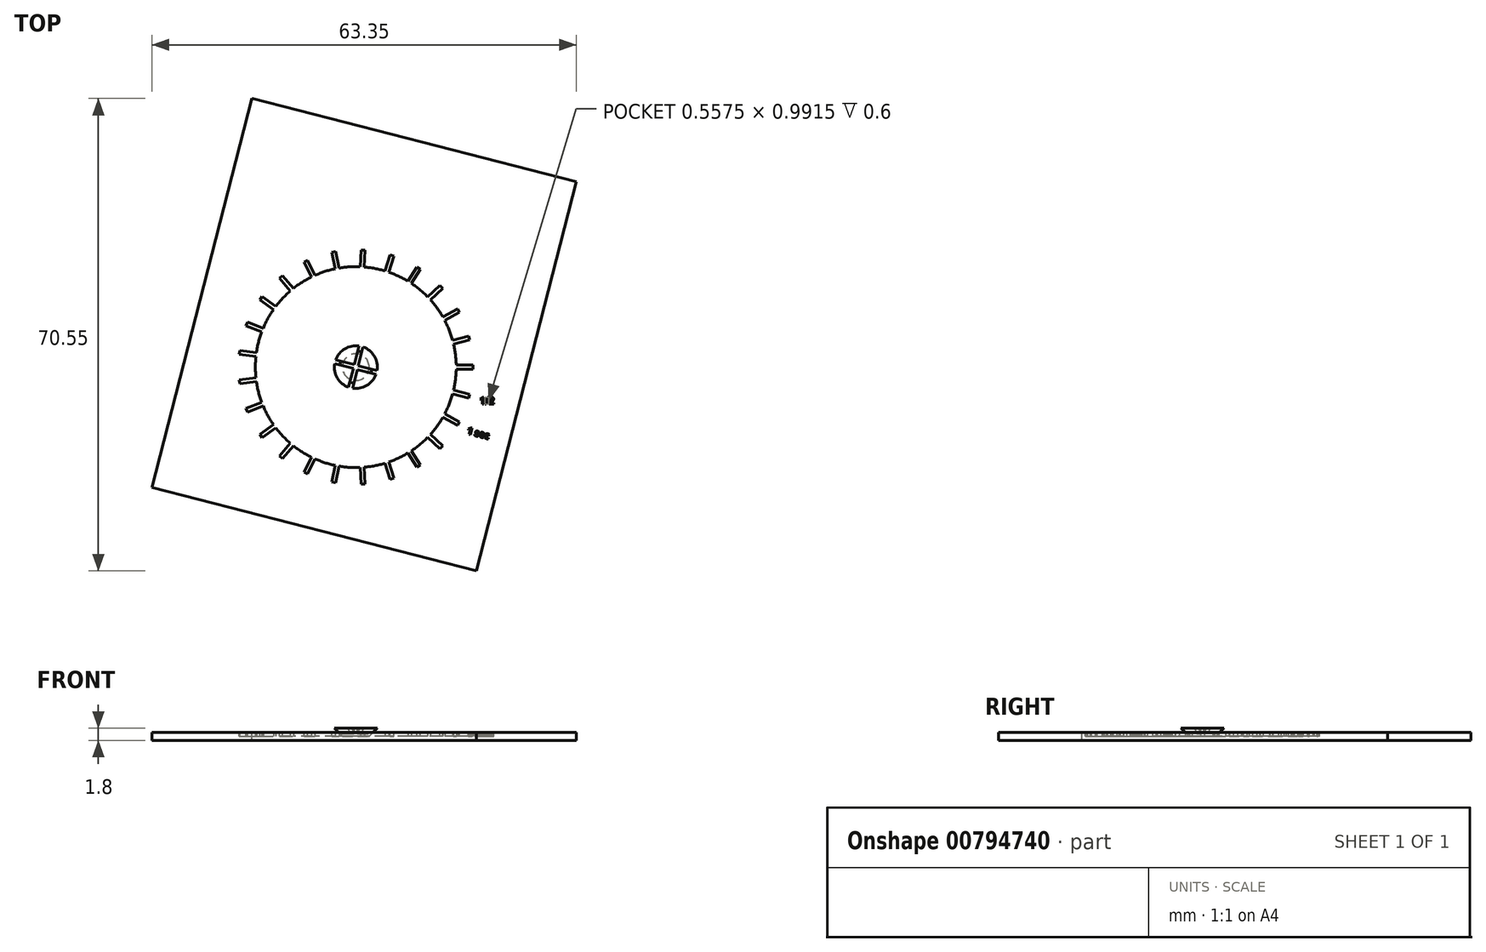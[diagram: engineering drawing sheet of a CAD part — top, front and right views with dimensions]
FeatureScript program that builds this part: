
annotation { "Feature Type Name" : "Feature", "Feature Type Description" : "" }
export const myFeature = defineFeature(function(context is Context, id is Id, definition is map)
    precondition{}
    {
        {
            var Q0;
            Q0=qCreatedBy(makeId("Top.planeOp"),FACE);
            var sketch = newSketch(context, id + "F0", { "sketchPlane" : qUnion([Q0])});
            skLineSegment(sketch, "E0.bottom", {"start": v(25, -30) * mm, "end": v(-25, -30) * mm});
            skLineSegment(sketch, "E0.top", {"start": v(25, 30) * mm, "end": v(-25, 30) * mm});
            skLineSegment(sketch, "E0.left", {"start": v(25, -30) * mm, "end": v(25, 30) * mm});
            skLineSegment(sketch, "E0.right", {"start": v(-25, -30) * mm, "end": v(-25, 30) * mm});
            skPoint(sketch, "E0.middle", {"position": v(0, 0) * mm});
            skCircle(sketch, "E1", {"center": v(0, -5) * mm, "radius": 15 * mm});
            skLineSegment(sketch, "E2", {"start": v(70, 36.13) * mm, "end": v(70, -44.16) * mm, "construction": true});
            skCircle(sketch, "E3", {"center": v(70, -12.38) * mm, "radius": 14.5 * mm});
            skLineSegment(sketch, "E4", {"start": v(70, -12.38) * mm, "end": v(87.5, -12.38) * mm, "construction": true});
            skLineSegment(sketch, "E5.bottom", {"start": v(82, -12.08) * mm, "end": v(87, -12.08) * mm});
            skLineSegment(sketch, "E5.top", {"start": v(82, -12.68) * mm, "end": v(87, -12.68) * mm});
            skLineSegment(sketch, "E5.left", {"start": v(82, -12.08) * mm, "end": v(82, -12.68) * mm});
            skLineSegment(sketch, "E5.right", {"start": v(87, -12.08) * mm, "end": v(87, -12.68) * mm});
            skSolve(sketch);
        }
        {
            var Q0;
            Q0=qCreatedBy(makeId("Right.planeOp"),FACE);
            var sketch = newSketch(context, id + "F1", { "sketchPlane" : qUnion([Q0])});
            skLineSegment(sketch, "E6", {"start": v(-5, 57.83) * mm, "end": v(-5, -48.42) * mm, "construction": true});
            skSolve(sketch);
        }
        {
            var Q0;
            Q0=makeQuery(id+"F0.imprint","IMPRINT",FACE,{"disambiguationData":[TD([[makeQuery(id+"F0.imprint","IMPRINT",EDGE,{"derivedFrom":sQuery(id+"F0.wireOp",EDGE,"E0.bottom")}),-1.0]])]});
            var Q1;
            Q1=makeQuery(id+"F0.imprint","IMPRINT",FACE,{"disambiguationData":[TD([[makeQuery(id+"F0.imprint","IMPRINT",EDGE,{"derivedFrom":sQuery(id+"F0.wireOp",EDGE,"E1")}),1.0]])]});
            extrude(context, id + "F2", {"entities" : qUnion([Q0, Q1]), "oppositeDirection" : true, "depth" : 0.6 * mm, "offsetDistance" : 25 * mm});
        }
        {
            var Q0;
            Q0=makeQuery(id+"F0.imprint","IMPRINT",FACE,{"disambiguationData":[TD([[makeQuery(id+"F0.imprint","IMPRINT",EDGE,{"derivedFrom":sQuery(id+"F0.wireOp",EDGE,"E0.bottom")}),-1.0]])]});
            extrude(context, id + "F3", {"entities" : qUnion([Q0]), "operationType" : NewBodyOperationType.ADD, "depth" : 0.6 * mm, "offsetDistance" : 25 * mm});
        }
        {
            var Q0;
            Q0=makeQuery(id+"F0.imprint","IMPRINT",FACE,{"disambiguationData":[TD([[makeQuery(id+"F0.imprint","IMPRINT",EDGE,{"derivedFrom":sQuery(id+"F0.wireOp",EDGE,"E1")}),1.0]])]});
            var sketch = newSketch(context, id + "F4", { "sketchPlane" : qUnion([Q0])});
            skCircle(sketch, "E7", {"center": v(0, -5) * mm, "radius": 2 * mm});
            skSolve(sketch);
        }
        {
            var Q0;
            Q0=makeQuery(id+"F4.imprint","IMPRINT",FACE,{"disambiguationData":[TD([[makeQuery(id+"F4.imprint","IMPRINT",EDGE,{"derivedFrom":sQuery(id+"F4.wireOp",EDGE,"E7")}),1.0]])]});
            extrude(context, id + "F5", {"entities" : qUnion([Q0]), "operationType" : NewBodyOperationType.ADD, "depth" : 1.2 * mm, "offsetDistance" : 25 * mm, "hasDraft" : true, "draftAngle" : 45 * degree});
        }
        {
            var Q0;
            Q0=makeQuery(id+"F5.opExtrude","CAP_FACE",FACE,{"disambiguationData":[OSD([sQuery(id+"F4.wireOp",EDGE,"E7")])],"isStart":false});
            var sketch = newSketch(context, id + "F6", { "sketchPlane" : qUnion([Q0])});
            skLineSegment(sketch, "E8.bottom", {"start": v(-0.3, 0) * mm, "end": v(0.3, 0) * mm});
            skLineSegment(sketch, "E8.top", {"start": v(-0.3, -10) * mm, "end": v(0.3, -10) * mm});
            skLineSegment(sketch, "E8.left", {"start": v(-0.3, 0) * mm, "end": v(-0.3, -10) * mm});
            skLineSegment(sketch, "E8.right", {"start": v(0.3, 0) * mm, "end": v(0.3, -10) * mm});
            skPoint(sketch, "E8.middle", {"position": v(0, -5) * mm});
            skLineSegment(sketch, "E9.bottom", {"start": v(-5, -4.7) * mm, "end": v(5, -4.7) * mm});
            skLineSegment(sketch, "E9.top", {"start": v(-5, -5.3) * mm, "end": v(5, -5.3) * mm});
            skLineSegment(sketch, "E9.left", {"start": v(-5, -4.7) * mm, "end": v(-5, -5.3) * mm});
            skLineSegment(sketch, "E9.right", {"start": v(5, -4.7) * mm, "end": v(5, -5.3) * mm});
            skSolve(sketch);
        }
        {
            var Q0;
            Q0 = qSketchRegion(id + "F6", true);
            extrude(context, id + "F7", {"entities" : qUnion([Q0]), "operationType" : NewBodyOperationType.REMOVE, "oppositeDirection" : true, "depth" : 0.8 * mm, "offsetDistance" : 25 * mm});
        }
        {
            var Q0;
            Q0=makeQuery(id+"F3.opExtrude","CAP_FACE",FACE,{"disambiguationData":[OSD([sQuery(id+"F0.wireOp",EDGE,"E0.bottom"),sQuery(id+"F0.wireOp",EDGE,"E0.top"),sQuery(id+"F0.wireOp",EDGE,"E0.left"),sQuery(id+"F0.wireOp",EDGE,"E0.right"),sQuery(id+"F0.wireOp",EDGE,"E1")])],"isStart":false});
            var sketch = newSketch(context, id + "F8", { "sketchPlane" : qUnion([Q0])});
            skLineSegment(sketch, "E10", {"start": v(0, 17.05) * mm, "end": v(0, -50.38) * mm, "construction": true});
            skLineSegment(sketch, "E11", {"start": v(-21.67, -5) * mm, "end": v(32.65, -5) * mm, "construction": true});
            skLineSegment(sketch, "E12.bottom", {"start": v(17.5, -4.7) * mm, "end": v(12.5, -4.7) * mm});
            skLineSegment(sketch, "E12.top", {"start": v(17.5, -5.3) * mm, "end": v(12.5, -5.3) * mm});
            skLineSegment(sketch, "E12.left", {"start": v(17.5, -4.7) * mm, "end": v(17.5, -5.3) * mm});
            skLineSegment(sketch, "E12.right", {"start": v(12.5, -4.7) * mm, "end": v(12.5, -5.3) * mm});
            skPoint(sketch, "E12.middle", {"position": v(15, -5) * mm});
            skLineSegment(sketch, "E13.1.0", {"start": v(16.88, -0.36) * mm, "end": v(12.03, -1.6) * mm});
            skLineSegment(sketch, "E13.1.1", {"start": v(17.02, -0.94) * mm, "end": v(12.18, -2.18) * mm});
            skLineSegment(sketch, "E13.1.2", {"start": v(16.88, -0.36) * mm, "end": v(17.02, -0.94) * mm});
            skLineSegment(sketch, "E13.1.3", {"start": v(12.03, -1.6) * mm, "end": v(12.18, -2.18) * mm});
            skLineSegment(sketch, "E13.2.0", {"start": v(15.2, 3.7) * mm, "end": v(10.8, 1.28) * mm});
            skLineSegment(sketch, "E13.2.1", {"start": v(15.48, 3.17) * mm, "end": v(11.1, 0.76) * mm});
            skLineSegment(sketch, "E13.2.2", {"start": v(15.2, 3.7) * mm, "end": v(15.48, 3.17) * mm});
            skLineSegment(sketch, "E13.2.3", {"start": v(10.8, 1.28) * mm, "end": v(11.1, 0.76) * mm});
            skLineSegment(sketch, "E13.3.0", {"start": v(12.55, 7.2) * mm, "end": v(8.9, 3.78) * mm});
            skLineSegment(sketch, "E13.3.1", {"start": v(12.96, 6.76) * mm, "end": v(9.32, 3.34) * mm});
            skLineSegment(sketch, "E13.3.2", {"start": v(12.55, 7.2) * mm, "end": v(12.96, 6.76) * mm});
            skLineSegment(sketch, "E13.3.3", {"start": v(8.9, 3.78) * mm, "end": v(9.32, 3.34) * mm});
            skLineSegment(sketch, "E13.4.0", {"start": v(9.12, 9.94) * mm, "end": v(6.44, 5.71) * mm});
            skLineSegment(sketch, "E13.4.1", {"start": v(9.63, 9.61) * mm, "end": v(6.95, 5.4) * mm});
            skLineSegment(sketch, "E13.4.2", {"start": v(9.12, 9.94) * mm, "end": v(9.63, 9.61) * mm});
            skLineSegment(sketch, "E13.4.3", {"start": v(6.44, 5.71) * mm, "end": v(6.95, 5.4) * mm});
            skLineSegment(sketch, "E13.5.0", {"start": v(5.12, 11.74) * mm, "end": v(3.58, 6.98) * mm});
            skLineSegment(sketch, "E13.5.1", {"start": v(5.7, 11.55) * mm, "end": v(4.15, 6.8) * mm});
            skLineSegment(sketch, "E13.5.2", {"start": v(5.12, 11.74) * mm, "end": v(5.7, 11.55) * mm});
            skLineSegment(sketch, "E13.5.3", {"start": v(3.58, 6.98) * mm, "end": v(4.15, 6.8) * mm});
            skLineSegment(sketch, "E13.6.0", {"start": v(0.8, 12.48) * mm, "end": v(0.49, 7.5) * mm});
            skLineSegment(sketch, "E13.6.1", {"start": v(1.4, 12.45) * mm, "end": v(1.08, 7.46) * mm});
            skLineSegment(sketch, "E13.6.2", {"start": v(0.8, 12.48) * mm, "end": v(1.4, 12.45) * mm});
            skLineSegment(sketch, "E13.6.3", {"start": v(0.49, 7.5) * mm, "end": v(1.08, 7.46) * mm});
            skLineSegment(sketch, "E13.7.0", {"start": v(-3.57, 12.13) * mm, "end": v(-2.64, 7.22) * mm});
            skLineSegment(sketch, "E13.7.1", {"start": v(-2.98, 12.25) * mm, "end": v(-2.05, 7.33) * mm});
            skLineSegment(sketch, "E13.7.2", {"start": v(-3.57, 12.13) * mm, "end": v(-2.98, 12.25) * mm});
            skLineSegment(sketch, "E13.7.3", {"start": v(-2.64, 7.22) * mm, "end": v(-2.05, 7.33) * mm});
            skLineSegment(sketch, "E13.8.0", {"start": v(-7.72, 10.7) * mm, "end": v(-5.6, 6.18) * mm});
            skLineSegment(sketch, "E13.8.1", {"start": v(-7.18, 10.96) * mm, "end": v(-5.05, 6.44) * mm});
            skLineSegment(sketch, "E13.8.2", {"start": v(-7.72, 10.7) * mm, "end": v(-7.18, 10.96) * mm});
            skLineSegment(sketch, "E13.8.3", {"start": v(-5.6, 6.18) * mm, "end": v(-5.05, 6.44) * mm});
            skLineSegment(sketch, "E13.9.0", {"start": v(-11.39, 8.3) * mm, "end": v(-8.2, 4.44) * mm});
            skLineSegment(sketch, "E13.9.1", {"start": v(-10.92, 8.68) * mm, "end": v(-7.74, 4.82) * mm});
            skLineSegment(sketch, "E13.9.2", {"start": v(-11.39, 8.3) * mm, "end": v(-10.92, 8.68) * mm});
            skLineSegment(sketch, "E13.9.3", {"start": v(-8.2, 4.44) * mm, "end": v(-7.74, 4.82) * mm});
            skLineSegment(sketch, "E13.10.0", {"start": v(-14.33, 5.04) * mm, "end": v(-10.29, 2.1) * mm});
            skLineSegment(sketch, "E13.10.1", {"start": v(-13.98, 5.53) * mm, "end": v(-9.94, 2.6) * mm});
            skLineSegment(sketch, "E13.10.2", {"start": v(-14.33, 5.04) * mm, "end": v(-13.98, 5.53) * mm});
            skLineSegment(sketch, "E13.10.3", {"start": v(-10.29, 2.1) * mm, "end": v(-9.94, 2.6) * mm});
            skLineSegment(sketch, "E13.11.0", {"start": v(-16.38, 1.16) * mm, "end": v(-11.73, -0.68) * mm});
            skLineSegment(sketch, "E13.11.1", {"start": v(-16.16, 1.72) * mm, "end": v(-11.51, -0.12) * mm});
            skLineSegment(sketch, "E13.11.2", {"start": v(-16.38, 1.16) * mm, "end": v(-16.16, 1.72) * mm});
            skLineSegment(sketch, "E13.11.3", {"start": v(-11.73, -0.68) * mm, "end": v(-11.51, -0.12) * mm});
            skLineSegment(sketch, "E13.12.0", {"start": v(-17.4, -3.1) * mm, "end": v(-12.44, -3.73) * mm});
            skLineSegment(sketch, "E13.12.1", {"start": v(-17.32, -2.5) * mm, "end": v(-12.36, -3.14) * mm});
            skLineSegment(sketch, "E13.12.2", {"start": v(-17.4, -3.1) * mm, "end": v(-17.32, -2.5) * mm});
            skLineSegment(sketch, "E13.12.3", {"start": v(-12.44, -3.73) * mm, "end": v(-12.36, -3.14) * mm});
            skLineSegment(sketch, "E13.13.0", {"start": v(-17.32, -7.5) * mm, "end": v(-12.36, -6.86) * mm});
            skLineSegment(sketch, "E13.13.1", {"start": v(-17.4, -6.9) * mm, "end": v(-12.44, -6.27) * mm});
            skLineSegment(sketch, "E13.13.2", {"start": v(-17.32, -7.5) * mm, "end": v(-17.4, -6.9) * mm});
            skLineSegment(sketch, "E13.13.3", {"start": v(-12.36, -6.86) * mm, "end": v(-12.44, -6.27) * mm});
            skLineSegment(sketch, "E13.14.0", {"start": v(-16.16, -11.72) * mm, "end": v(-11.51, -9.88) * mm});
            skLineSegment(sketch, "E13.14.1", {"start": v(-16.38, -11.16) * mm, "end": v(-11.73, -9.32) * mm});
            skLineSegment(sketch, "E13.14.2", {"start": v(-16.16, -11.72) * mm, "end": v(-16.38, -11.16) * mm});
            skLineSegment(sketch, "E13.14.3", {"start": v(-11.51, -9.88) * mm, "end": v(-11.73, -9.32) * mm});
            skLineSegment(sketch, "E13.15.0", {"start": v(-13.98, -15.53) * mm, "end": v(-9.94, -12.6) * mm});
            skLineSegment(sketch, "E13.15.1", {"start": v(-14.33, -15.04) * mm, "end": v(-10.29, -12.1) * mm});
            skLineSegment(sketch, "E13.15.2", {"start": v(-13.98, -15.53) * mm, "end": v(-14.33, -15.04) * mm});
            skLineSegment(sketch, "E13.15.3", {"start": v(-9.94, -12.6) * mm, "end": v(-10.29, -12.1) * mm});
            skLineSegment(sketch, "E13.16.0", {"start": v(-10.92, -18.68) * mm, "end": v(-7.74, -14.82) * mm});
            skLineSegment(sketch, "E13.16.1", {"start": v(-11.39, -18.3) * mm, "end": v(-8.2, -14.44) * mm});
            skLineSegment(sketch, "E13.16.2", {"start": v(-10.92, -18.68) * mm, "end": v(-11.39, -18.3) * mm});
            skLineSegment(sketch, "E13.16.3", {"start": v(-7.74, -14.82) * mm, "end": v(-8.2, -14.44) * mm});
            skLineSegment(sketch, "E13.17.0", {"start": v(-7.18, -20.96) * mm, "end": v(-5.05, -16.44) * mm});
            skLineSegment(sketch, "E13.17.1", {"start": v(-7.72, -20.7) * mm, "end": v(-5.6, -16.18) * mm});
            skLineSegment(sketch, "E13.17.2", {"start": v(-7.18, -20.96) * mm, "end": v(-7.72, -20.7) * mm});
            skLineSegment(sketch, "E13.17.3", {"start": v(-5.05, -16.44) * mm, "end": v(-5.6, -16.18) * mm});
            skLineSegment(sketch, "E13.18.0", {"start": v(-2.98, -22.25) * mm, "end": v(-2.05, -17.33) * mm});
            skLineSegment(sketch, "E13.18.1", {"start": v(-3.57, -22.13) * mm, "end": v(-2.64, -17.22) * mm});
            skLineSegment(sketch, "E13.18.2", {"start": v(-2.98, -22.25) * mm, "end": v(-3.57, -22.13) * mm});
            skLineSegment(sketch, "E13.18.3", {"start": v(-2.05, -17.33) * mm, "end": v(-2.64, -17.22) * mm});
            skLineSegment(sketch, "E13.19.0", {"start": v(1.4, -22.45) * mm, "end": v(1.08, -17.46) * mm});
            skLineSegment(sketch, "E13.19.1", {"start": v(0.8, -22.48) * mm, "end": v(0.49, -17.5) * mm});
            skLineSegment(sketch, "E13.19.2", {"start": v(1.4, -22.45) * mm, "end": v(0.8, -22.48) * mm});
            skLineSegment(sketch, "E13.19.3", {"start": v(1.08, -17.46) * mm, "end": v(0.49, -17.5) * mm});
            skLineSegment(sketch, "E13.20.0", {"start": v(5.7, -21.55) * mm, "end": v(4.15, -16.8) * mm});
            skLineSegment(sketch, "E13.20.1", {"start": v(5.12, -21.74) * mm, "end": v(3.58, -16.98) * mm});
            skLineSegment(sketch, "E13.20.2", {"start": v(5.7, -21.55) * mm, "end": v(5.12, -21.74) * mm});
            skLineSegment(sketch, "E13.20.3", {"start": v(4.15, -16.8) * mm, "end": v(3.58, -16.98) * mm});
            skLineSegment(sketch, "E13.21.0", {"start": v(9.63, -19.61) * mm, "end": v(6.95, -15.4) * mm});
            skLineSegment(sketch, "E13.21.1", {"start": v(9.12, -19.94) * mm, "end": v(6.44, -15.71) * mm});
            skLineSegment(sketch, "E13.21.2", {"start": v(9.63, -19.61) * mm, "end": v(9.12, -19.94) * mm});
            skLineSegment(sketch, "E13.21.3", {"start": v(6.95, -15.4) * mm, "end": v(6.44, -15.71) * mm});
            skLineSegment(sketch, "E13.22.0", {"start": v(12.96, -16.76) * mm, "end": v(9.32, -13.34) * mm});
            skLineSegment(sketch, "E13.22.1", {"start": v(12.55, -17.2) * mm, "end": v(8.9, -13.78) * mm});
            skLineSegment(sketch, "E13.22.2", {"start": v(12.96, -16.76) * mm, "end": v(12.55, -17.2) * mm});
            skLineSegment(sketch, "E13.22.3", {"start": v(9.32, -13.34) * mm, "end": v(8.9, -13.78) * mm});
            skLineSegment(sketch, "E13.23.0", {"start": v(15.48, -13.17) * mm, "end": v(11.1, -10.76) * mm});
            skLineSegment(sketch, "E13.23.1", {"start": v(15.2, -13.7) * mm, "end": v(10.8, -11.28) * mm});
            skLineSegment(sketch, "E13.23.2", {"start": v(15.48, -13.17) * mm, "end": v(15.2, -13.7) * mm});
            skLineSegment(sketch, "E13.23.3", {"start": v(11.1, -10.76) * mm, "end": v(10.8, -11.28) * mm});
            skLineSegment(sketch, "E13.24.0", {"start": v(17.02, -9.06) * mm, "end": v(12.18, -7.82) * mm});
            skLineSegment(sketch, "E13.24.1", {"start": v(16.88, -9.64) * mm, "end": v(12.03, -8.4) * mm});
            skLineSegment(sketch, "E13.24.2", {"start": v(17.02, -9.06) * mm, "end": v(16.88, -9.64) * mm});
            skLineSegment(sketch, "E13.24.3", {"start": v(12.18, -7.82) * mm, "end": v(12.03, -8.4) * mm});
            skPoint(sketch, "E13.center", {"position": v(0, -5) * mm});
            skSolve(sketch);
        }
        {
            var Q0;
            Q0 = qSketchRegion(id + "F8", true);
            extrude(context, id + "F9", {"entities" : qUnion([Q0]), "operationType" : NewBodyOperationType.REMOVE, "oppositeDirection" : true, "depth" : 0.6 * mm, "offsetDistance" : 25 * mm});
        }
        {
            var Q0;
            {var subQ113=sQuery(id+"F8.wireOp",EDGE,"E12.left");Q0=makeQuery(id+"F8.imprint","IMPRINT",FACE,{"disambiguationData":[TD([[makeQuery(id+"F8.imprint","IMPRINT",EDGE,{"derivedFrom":subQ113}),1.0]])]});}
            var sketch = newSketch(context, id + "F10", { "sketchPlane" : qUnion([Q0])});
            skText(sketch, "E14", { "text": "1 sec", "fontName": "OpenSans-Bold.ttf"});
            const initialGuessF10  = {"E14": [0.0185, -0.0105, 1, 0, 0.001]};
            skSetInitialGuess(sketch, initialGuessF10);
            skSolve(sketch);
        }
        {
            var Q0;
            Q0 = qSketchRegion(id + "F10", true);
            var Q1;
            Q1=makeQuery(id+"F9.boolean.opBoolean","MERGE",FACE,{"derivedFrom":[makeQuery(id+"F2.opExtrude","CAP_FACE",FACE,{"disambiguationData":[OSD([sQuery(id+"F0.wireOp",EDGE,"E0.bottom"),sQuery(id+"F0.wireOp",EDGE,"E0.top"),sQuery(id+"F0.wireOp",EDGE,"E0.left"),sQuery(id+"F0.wireOp",EDGE,"E0.right")])],"isStart":true}),makeQuery(id+"F9.opExtrude","CAP_FACE",FACE,{"disambiguationData":[OSD([sQuery(id+"F8.wireOp",EDGE,"E12.bottom"),sQuery(id+"F8.wireOp",EDGE,"E12.top"),sQuery(id+"F8.wireOp",EDGE,"E12.left"),sQuery(id+"F8.wireOp",EDGE,"E12.right")])],"isStart":false}),makeQuery(id+"F9.opExtrude","CAP_FACE",FACE,{"disambiguationData":[OSD([sQuery(id+"F8.wireOp",EDGE,"E13.1.0"),sQuery(id+"F8.wireOp",EDGE,"E13.1.1"),sQuery(id+"F8.wireOp",EDGE,"E13.1.2"),sQuery(id+"F8.wireOp",EDGE,"E13.1.3")])],"isStart":false}),makeQuery(id+"F9.opExtrude","CAP_FACE",FACE,{"disambiguationData":[OSD([sQuery(id+"F8.wireOp",EDGE,"E13.2.0"),sQuery(id+"F8.wireOp",EDGE,"E13.2.1"),sQuery(id+"F8.wireOp",EDGE,"E13.2.2"),sQuery(id+"F8.wireOp",EDGE,"E13.2.3")])],"isStart":false}),makeQuery(id+"F9.opExtrude","CAP_FACE",FACE,{"disambiguationData":[OSD([sQuery(id+"F8.wireOp",EDGE,"E13.3.0"),sQuery(id+"F8.wireOp",EDGE,"E13.3.1"),sQuery(id+"F8.wireOp",EDGE,"E13.3.2"),sQuery(id+"F8.wireOp",EDGE,"E13.3.3")])],"isStart":false}),makeQuery(id+"F9.opExtrude","CAP_FACE",FACE,{"disambiguationData":[OSD([sQuery(id+"F8.wireOp",EDGE,"E13.4.0"),sQuery(id+"F8.wireOp",EDGE,"E13.4.1"),sQuery(id+"F8.wireOp",EDGE,"E13.4.2"),sQuery(id+"F8.wireOp",EDGE,"E13.4.3")])],"isStart":false}),makeQuery(id+"F9.opExtrude","CAP_FACE",FACE,{"disambiguationData":[OSD([sQuery(id+"F8.wireOp",EDGE,"E13.5.0"),sQuery(id+"F8.wireOp",EDGE,"E13.5.1"),sQuery(id+"F8.wireOp",EDGE,"E13.5.2"),sQuery(id+"F8.wireOp",EDGE,"E13.5.3")])],"isStart":false}),makeQuery(id+"F9.opExtrude","CAP_FACE",FACE,{"disambiguationData":[OSD([sQuery(id+"F8.wireOp",EDGE,"E13.6.0"),sQuery(id+"F8.wireOp",EDGE,"E13.6.1"),sQuery(id+"F8.wireOp",EDGE,"E13.6.2"),sQuery(id+"F8.wireOp",EDGE,"E13.6.3")])],"isStart":false}),makeQuery(id+"F9.opExtrude","CAP_FACE",FACE,{"disambiguationData":[OSD([sQuery(id+"F8.wireOp",EDGE,"E13.7.0"),sQuery(id+"F8.wireOp",EDGE,"E13.7.1"),sQuery(id+"F8.wireOp",EDGE,"E13.7.2"),sQuery(id+"F8.wireOp",EDGE,"E13.7.3")])],"isStart":false}),makeQuery(id+"F9.opExtrude","CAP_FACE",FACE,{"disambiguationData":[OSD([sQuery(id+"F8.wireOp",EDGE,"E13.8.0"),sQuery(id+"F8.wireOp",EDGE,"E13.8.1"),sQuery(id+"F8.wireOp",EDGE,"E13.8.2"),sQuery(id+"F8.wireOp",EDGE,"E13.8.3")])],"isStart":false}),makeQuery(id+"F9.opExtrude","CAP_FACE",FACE,{"disambiguationData":[OSD([sQuery(id+"F8.wireOp",EDGE,"E13.9.0"),sQuery(id+"F8.wireOp",EDGE,"E13.9.1"),sQuery(id+"F8.wireOp",EDGE,"E13.9.2"),sQuery(id+"F8.wireOp",EDGE,"E13.9.3")])],"isStart":false}),makeQuery(id+"F9.opExtrude","CAP_FACE",FACE,{"disambiguationData":[OSD([sQuery(id+"F8.wireOp",EDGE,"E13.10.0"),sQuery(id+"F8.wireOp",EDGE,"E13.10.1"),sQuery(id+"F8.wireOp",EDGE,"E13.10.2"),sQuery(id+"F8.wireOp",EDGE,"E13.10.3")])],"isStart":false}),makeQuery(id+"F9.opExtrude","CAP_FACE",FACE,{"disambiguationData":[OSD([sQuery(id+"F8.wireOp",EDGE,"E13.11.0"),sQuery(id+"F8.wireOp",EDGE,"E13.11.1"),sQuery(id+"F8.wireOp",EDGE,"E13.11.2"),sQuery(id+"F8.wireOp",EDGE,"E13.11.3")])],"isStart":false}),makeQuery(id+"F9.opExtrude","CAP_FACE",FACE,{"disambiguationData":[OSD([sQuery(id+"F8.wireOp",EDGE,"E13.12.0"),sQuery(id+"F8.wireOp",EDGE,"E13.12.1"),sQuery(id+"F8.wireOp",EDGE,"E13.12.2"),sQuery(id+"F8.wireOp",EDGE,"E13.12.3")])],"isStart":false}),makeQuery(id+"F9.opExtrude","CAP_FACE",FACE,{"disambiguationData":[OSD([sQuery(id+"F8.wireOp",EDGE,"E13.13.0"),sQuery(id+"F8.wireOp",EDGE,"E13.13.1"),sQuery(id+"F8.wireOp",EDGE,"E13.13.2"),sQuery(id+"F8.wireOp",EDGE,"E13.13.3")])],"isStart":false}),makeQuery(id+"F9.opExtrude","CAP_FACE",FACE,{"disambiguationData":[OSD([sQuery(id+"F8.wireOp",EDGE,"E13.14.0"),sQuery(id+"F8.wireOp",EDGE,"E13.14.1"),sQuery(id+"F8.wireOp",EDGE,"E13.14.2"),sQuery(id+"F8.wireOp",EDGE,"E13.14.3")])],"isStart":false}),makeQuery(id+"F9.opExtrude","CAP_FACE",FACE,{"disambiguationData":[OSD([sQuery(id+"F8.wireOp",EDGE,"E13.15.0"),sQuery(id+"F8.wireOp",EDGE,"E13.15.1"),sQuery(id+"F8.wireOp",EDGE,"E13.15.2"),sQuery(id+"F8.wireOp",EDGE,"E13.15.3")])],"isStart":false}),makeQuery(id+"F9.opExtrude","CAP_FACE",FACE,{"disambiguationData":[OSD([sQuery(id+"F8.wireOp",EDGE,"E13.16.0"),sQuery(id+"F8.wireOp",EDGE,"E13.16.1"),sQuery(id+"F8.wireOp",EDGE,"E13.16.2"),sQuery(id+"F8.wireOp",EDGE,"E13.16.3")])],"isStart":false}),makeQuery(id+"F9.opExtrude","CAP_FACE",FACE,{"disambiguationData":[OSD([sQuery(id+"F8.wireOp",EDGE,"E13.17.0"),sQuery(id+"F8.wireOp",EDGE,"E13.17.1"),sQuery(id+"F8.wireOp",EDGE,"E13.17.2"),sQuery(id+"F8.wireOp",EDGE,"E13.17.3")])],"isStart":false}),makeQuery(id+"F9.opExtrude","CAP_FACE",FACE,{"disambiguationData":[OSD([sQuery(id+"F8.wireOp",EDGE,"E13.18.0"),sQuery(id+"F8.wireOp",EDGE,"E13.18.1"),sQuery(id+"F8.wireOp",EDGE,"E13.18.2"),sQuery(id+"F8.wireOp",EDGE,"E13.18.3")])],"isStart":false}),makeQuery(id+"F9.opExtrude","CAP_FACE",FACE,{"disambiguationData":[OSD([sQuery(id+"F8.wireOp",EDGE,"E13.19.0"),sQuery(id+"F8.wireOp",EDGE,"E13.19.1"),sQuery(id+"F8.wireOp",EDGE,"E13.19.2"),sQuery(id+"F8.wireOp",EDGE,"E13.19.3")])],"isStart":false}),makeQuery(id+"F9.opExtrude","CAP_FACE",FACE,{"disambiguationData":[OSD([sQuery(id+"F8.wireOp",EDGE,"E13.20.0"),sQuery(id+"F8.wireOp",EDGE,"E13.20.1"),sQuery(id+"F8.wireOp",EDGE,"E13.20.2"),sQuery(id+"F8.wireOp",EDGE,"E13.20.3")])],"isStart":false}),makeQuery(id+"F9.opExtrude","CAP_FACE",FACE,{"disambiguationData":[OSD([sQuery(id+"F8.wireOp",EDGE,"E13.21.0"),sQuery(id+"F8.wireOp",EDGE,"E13.21.1"),sQuery(id+"F8.wireOp",EDGE,"E13.21.2"),sQuery(id+"F8.wireOp",EDGE,"E13.21.3")])],"isStart":false}),makeQuery(id+"F9.opExtrude","CAP_FACE",FACE,{"disambiguationData":[OSD([sQuery(id+"F8.wireOp",EDGE,"E13.22.0"),sQuery(id+"F8.wireOp",EDGE,"E13.22.1"),sQuery(id+"F8.wireOp",EDGE,"E13.22.2"),sQuery(id+"F8.wireOp",EDGE,"E13.22.3")])],"isStart":false}),makeQuery(id+"F9.opExtrude","CAP_FACE",FACE,{"disambiguationData":[OSD([sQuery(id+"F8.wireOp",EDGE,"E13.23.0"),sQuery(id+"F8.wireOp",EDGE,"E13.23.1"),sQuery(id+"F8.wireOp",EDGE,"E13.23.2"),sQuery(id+"F8.wireOp",EDGE,"E13.23.3")])],"isStart":false}),makeQuery(id+"F9.opExtrude","CAP_FACE",FACE,{"disambiguationData":[OSD([sQuery(id+"F8.wireOp",EDGE,"E13.24.0"),sQuery(id+"F8.wireOp",EDGE,"E13.24.1"),sQuery(id+"F8.wireOp",EDGE,"E13.24.2"),sQuery(id+"F8.wireOp",EDGE,"E13.24.3")])],"isStart":false})]});
            extrude(context, id + "F11", {"entities" : qUnion([Q0]), "operationType" : NewBodyOperationType.REMOVE, "endBound" : BoundingType.UP_TO_SURFACE, "oppositeDirection" : true, "depth" : 0.6 * mm, "endBoundEntityFace" : qUnion([Q1]), "offsetDistance" : 25 * mm});
        }
        {
            var Q0;
            Q0=makeQuery(id+"F2.opExtrude","SWEPT_BODY",BODY,{"disambiguationData":[OSD([sQuery(id+"F0.wireOp",EDGE,"E0.bottom"),sQuery(id+"F0.wireOp",EDGE,"E0.top"),sQuery(id+"F0.wireOp",EDGE,"E0.left"),sQuery(id+"F0.wireOp",EDGE,"E0.right")])]});
            var Q1;
            Q1=sQuery(id+"F1.wireOp",EDGE,"E6");
            transform(context, id + "F12", {"entities" : qUnion([Q0]), "transformType" : TransformType.ROTATION, "transformAxis" : qUnion([Q1]), "angle" : 14.4 * degree, "makeCopy" : false});
        }
        {
            var Q0;
            {var subQ0=sQuery(id+"F0.wireOp",EDGE,"E1");var subQ1=sQuery(id+"F0.wireOp",EDGE,"E0.right");var subQ2=sQuery(id+"F0.wireOp",EDGE,"E0.left");var subQ3=sQuery(id+"F0.wireOp",EDGE,"E0.top");var subQ4=sQuery(id+"F0.wireOp",EDGE,"E0.bottom");Q0=makeQuery(id+"F11.boolean.opBoolean","SPLIT",FACE,{"disambiguationData":[TD([makeQuery(id+"F2.opExtrude","SWEPT_FACE",FACE,{"disambiguationData":[OSD([subQ4])]})])],"derivedFrom":makeQuery(id+"F3.opExtrude","CAP_FACE",FACE,{"disambiguationData":[OSD([subQ4,subQ3,subQ2,subQ1,subQ0])],"isStart":false})});}
            var sketch = newSketch(context, id + "F13", { "sketchPlane" : qUnion([Q0])});
            skText(sketch, "E15", { "text": "1/2", "fontName": "OpenSans-Bold.ttf"});
            const initialGuessF13  = {"E15": [0.0185, -0.0105, 1, 0, 0.001]};
            skSetInitialGuess(sketch, initialGuessF13);
            skSolve(sketch);
        }
        {
            var Q0;
            Q0 = qSketchRegion(id + "F13", true);
            var Q1;
            Q1=makeQuery(id+"F9.boolean.opBoolean","MERGE",FACE,{"derivedFrom":[makeQuery(id+"F2.opExtrude","CAP_FACE",FACE,{"disambiguationData":[OSD([sQuery(id+"F0.wireOp",EDGE,"E0.bottom"),sQuery(id+"F0.wireOp",EDGE,"E0.top"),sQuery(id+"F0.wireOp",EDGE,"E0.left"),sQuery(id+"F0.wireOp",EDGE,"E0.right")])],"isStart":true}),makeQuery(id+"F9.opExtrude","CAP_FACE",FACE,{"disambiguationData":[OSD([sQuery(id+"F8.wireOp",EDGE,"E12.bottom"),sQuery(id+"F8.wireOp",EDGE,"E12.top"),sQuery(id+"F8.wireOp",EDGE,"E12.left"),sQuery(id+"F8.wireOp",EDGE,"E12.right")])],"isStart":false}),makeQuery(id+"F9.opExtrude","CAP_FACE",FACE,{"disambiguationData":[OSD([sQuery(id+"F8.wireOp",EDGE,"E13.1.0"),sQuery(id+"F8.wireOp",EDGE,"E13.1.1"),sQuery(id+"F8.wireOp",EDGE,"E13.1.2"),sQuery(id+"F8.wireOp",EDGE,"E13.1.3")])],"isStart":false}),makeQuery(id+"F9.opExtrude","CAP_FACE",FACE,{"disambiguationData":[OSD([sQuery(id+"F8.wireOp",EDGE,"E13.2.0"),sQuery(id+"F8.wireOp",EDGE,"E13.2.1"),sQuery(id+"F8.wireOp",EDGE,"E13.2.2"),sQuery(id+"F8.wireOp",EDGE,"E13.2.3")])],"isStart":false}),makeQuery(id+"F9.opExtrude","CAP_FACE",FACE,{"disambiguationData":[OSD([sQuery(id+"F8.wireOp",EDGE,"E13.3.0"),sQuery(id+"F8.wireOp",EDGE,"E13.3.1"),sQuery(id+"F8.wireOp",EDGE,"E13.3.2"),sQuery(id+"F8.wireOp",EDGE,"E13.3.3")])],"isStart":false}),makeQuery(id+"F9.opExtrude","CAP_FACE",FACE,{"disambiguationData":[OSD([sQuery(id+"F8.wireOp",EDGE,"E13.4.0"),sQuery(id+"F8.wireOp",EDGE,"E13.4.1"),sQuery(id+"F8.wireOp",EDGE,"E13.4.2"),sQuery(id+"F8.wireOp",EDGE,"E13.4.3")])],"isStart":false}),makeQuery(id+"F9.opExtrude","CAP_FACE",FACE,{"disambiguationData":[OSD([sQuery(id+"F8.wireOp",EDGE,"E13.5.0"),sQuery(id+"F8.wireOp",EDGE,"E13.5.1"),sQuery(id+"F8.wireOp",EDGE,"E13.5.2"),sQuery(id+"F8.wireOp",EDGE,"E13.5.3")])],"isStart":false}),makeQuery(id+"F9.opExtrude","CAP_FACE",FACE,{"disambiguationData":[OSD([sQuery(id+"F8.wireOp",EDGE,"E13.6.0"),sQuery(id+"F8.wireOp",EDGE,"E13.6.1"),sQuery(id+"F8.wireOp",EDGE,"E13.6.2"),sQuery(id+"F8.wireOp",EDGE,"E13.6.3")])],"isStart":false}),makeQuery(id+"F9.opExtrude","CAP_FACE",FACE,{"disambiguationData":[OSD([sQuery(id+"F8.wireOp",EDGE,"E13.7.0"),sQuery(id+"F8.wireOp",EDGE,"E13.7.1"),sQuery(id+"F8.wireOp",EDGE,"E13.7.2"),sQuery(id+"F8.wireOp",EDGE,"E13.7.3")])],"isStart":false}),makeQuery(id+"F9.opExtrude","CAP_FACE",FACE,{"disambiguationData":[OSD([sQuery(id+"F8.wireOp",EDGE,"E13.8.0"),sQuery(id+"F8.wireOp",EDGE,"E13.8.1"),sQuery(id+"F8.wireOp",EDGE,"E13.8.2"),sQuery(id+"F8.wireOp",EDGE,"E13.8.3")])],"isStart":false}),makeQuery(id+"F9.opExtrude","CAP_FACE",FACE,{"disambiguationData":[OSD([sQuery(id+"F8.wireOp",EDGE,"E13.9.0"),sQuery(id+"F8.wireOp",EDGE,"E13.9.1"),sQuery(id+"F8.wireOp",EDGE,"E13.9.2"),sQuery(id+"F8.wireOp",EDGE,"E13.9.3")])],"isStart":false}),makeQuery(id+"F9.opExtrude","CAP_FACE",FACE,{"disambiguationData":[OSD([sQuery(id+"F8.wireOp",EDGE,"E13.10.0"),sQuery(id+"F8.wireOp",EDGE,"E13.10.1"),sQuery(id+"F8.wireOp",EDGE,"E13.10.2"),sQuery(id+"F8.wireOp",EDGE,"E13.10.3")])],"isStart":false}),makeQuery(id+"F9.opExtrude","CAP_FACE",FACE,{"disambiguationData":[OSD([sQuery(id+"F8.wireOp",EDGE,"E13.11.0"),sQuery(id+"F8.wireOp",EDGE,"E13.11.1"),sQuery(id+"F8.wireOp",EDGE,"E13.11.2"),sQuery(id+"F8.wireOp",EDGE,"E13.11.3")])],"isStart":false}),makeQuery(id+"F9.opExtrude","CAP_FACE",FACE,{"disambiguationData":[OSD([sQuery(id+"F8.wireOp",EDGE,"E13.12.0"),sQuery(id+"F8.wireOp",EDGE,"E13.12.1"),sQuery(id+"F8.wireOp",EDGE,"E13.12.2"),sQuery(id+"F8.wireOp",EDGE,"E13.12.3")])],"isStart":false}),makeQuery(id+"F9.opExtrude","CAP_FACE",FACE,{"disambiguationData":[OSD([sQuery(id+"F8.wireOp",EDGE,"E13.13.0"),sQuery(id+"F8.wireOp",EDGE,"E13.13.1"),sQuery(id+"F8.wireOp",EDGE,"E13.13.2"),sQuery(id+"F8.wireOp",EDGE,"E13.13.3")])],"isStart":false}),makeQuery(id+"F9.opExtrude","CAP_FACE",FACE,{"disambiguationData":[OSD([sQuery(id+"F8.wireOp",EDGE,"E13.14.0"),sQuery(id+"F8.wireOp",EDGE,"E13.14.1"),sQuery(id+"F8.wireOp",EDGE,"E13.14.2"),sQuery(id+"F8.wireOp",EDGE,"E13.14.3")])],"isStart":false}),makeQuery(id+"F9.opExtrude","CAP_FACE",FACE,{"disambiguationData":[OSD([sQuery(id+"F8.wireOp",EDGE,"E13.15.0"),sQuery(id+"F8.wireOp",EDGE,"E13.15.1"),sQuery(id+"F8.wireOp",EDGE,"E13.15.2"),sQuery(id+"F8.wireOp",EDGE,"E13.15.3")])],"isStart":false}),makeQuery(id+"F9.opExtrude","CAP_FACE",FACE,{"disambiguationData":[OSD([sQuery(id+"F8.wireOp",EDGE,"E13.16.0"),sQuery(id+"F8.wireOp",EDGE,"E13.16.1"),sQuery(id+"F8.wireOp",EDGE,"E13.16.2"),sQuery(id+"F8.wireOp",EDGE,"E13.16.3")])],"isStart":false}),makeQuery(id+"F9.opExtrude","CAP_FACE",FACE,{"disambiguationData":[OSD([sQuery(id+"F8.wireOp",EDGE,"E13.17.0"),sQuery(id+"F8.wireOp",EDGE,"E13.17.1"),sQuery(id+"F8.wireOp",EDGE,"E13.17.2"),sQuery(id+"F8.wireOp",EDGE,"E13.17.3")])],"isStart":false}),makeQuery(id+"F9.opExtrude","CAP_FACE",FACE,{"disambiguationData":[OSD([sQuery(id+"F8.wireOp",EDGE,"E13.18.0"),sQuery(id+"F8.wireOp",EDGE,"E13.18.1"),sQuery(id+"F8.wireOp",EDGE,"E13.18.2"),sQuery(id+"F8.wireOp",EDGE,"E13.18.3")])],"isStart":false}),makeQuery(id+"F9.opExtrude","CAP_FACE",FACE,{"disambiguationData":[OSD([sQuery(id+"F8.wireOp",EDGE,"E13.19.0"),sQuery(id+"F8.wireOp",EDGE,"E13.19.1"),sQuery(id+"F8.wireOp",EDGE,"E13.19.2"),sQuery(id+"F8.wireOp",EDGE,"E13.19.3")])],"isStart":false}),makeQuery(id+"F9.opExtrude","CAP_FACE",FACE,{"disambiguationData":[OSD([sQuery(id+"F8.wireOp",EDGE,"E13.20.0"),sQuery(id+"F8.wireOp",EDGE,"E13.20.1"),sQuery(id+"F8.wireOp",EDGE,"E13.20.2"),sQuery(id+"F8.wireOp",EDGE,"E13.20.3")])],"isStart":false}),makeQuery(id+"F9.opExtrude","CAP_FACE",FACE,{"disambiguationData":[OSD([sQuery(id+"F8.wireOp",EDGE,"E13.21.0"),sQuery(id+"F8.wireOp",EDGE,"E13.21.1"),sQuery(id+"F8.wireOp",EDGE,"E13.21.2"),sQuery(id+"F8.wireOp",EDGE,"E13.21.3")])],"isStart":false}),makeQuery(id+"F9.opExtrude","CAP_FACE",FACE,{"disambiguationData":[OSD([sQuery(id+"F8.wireOp",EDGE,"E13.22.0"),sQuery(id+"F8.wireOp",EDGE,"E13.22.1"),sQuery(id+"F8.wireOp",EDGE,"E13.22.2"),sQuery(id+"F8.wireOp",EDGE,"E13.22.3")])],"isStart":false}),makeQuery(id+"F9.opExtrude","CAP_FACE",FACE,{"disambiguationData":[OSD([sQuery(id+"F8.wireOp",EDGE,"E13.23.0"),sQuery(id+"F8.wireOp",EDGE,"E13.23.1"),sQuery(id+"F8.wireOp",EDGE,"E13.23.2"),sQuery(id+"F8.wireOp",EDGE,"E13.23.3")])],"isStart":false}),makeQuery(id+"F9.opExtrude","CAP_FACE",FACE,{"disambiguationData":[OSD([sQuery(id+"F8.wireOp",EDGE,"E13.24.0"),sQuery(id+"F8.wireOp",EDGE,"E13.24.1"),sQuery(id+"F8.wireOp",EDGE,"E13.24.2"),sQuery(id+"F8.wireOp",EDGE,"E13.24.3")])],"isStart":false})]});
            extrude(context, id + "F14", {"entities" : qUnion([Q0]), "operationType" : NewBodyOperationType.REMOVE, "endBound" : BoundingType.UP_TO_SURFACE, "oppositeDirection" : true, "depth" : 0.6 * mm, "endBoundEntityFace" : qUnion([Q1]), "offsetDistance" : 25 * mm});
        }
    });
